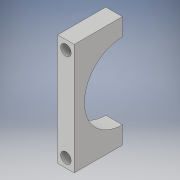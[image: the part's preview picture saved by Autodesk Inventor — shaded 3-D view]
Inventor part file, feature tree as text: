
AUTODESK INVENTOR PART (.ipt)
format: ipt  version: 2019 (Build 230136000, 136)  size: 118,272 bytes
history: native  units: mm
features: sketch x3, extrude x2, hole x1
ambient origin geometry x8: Origin, YZ Plane, XZ Plane, XY Plane, X Axis, Y Axis, Z Axis, Center Point
bodies: Body1 (feature_tree)
feature tree (6):
  sketch  "Sketch1"  dims[d2=50.0mm d7=5.5mm]
  extrude  "Extrusion4"  Depth=5.5mm
  hole  "Hole3"  [1 undecoded]
  extrude  "Extrusion5"  Depth=5.5mm
  sketch  "Sketch6"  dims[d8=37.0mm d9=31.0mm]
  sketch  "Sketch7"  dims[d10=3.0mm d11=2.75mm d45=5.5mm d46=37.0mm d47=31.0mm d48=3.0mm d49=2.75mm d50=16.0mm d51=0.0mm d52=3.5mm d53=6.0mm d54=4.0mm d55=2.0mm d56=90.0deg d57=8.0mm d58=20.594885mm d59=25.25mm d60=5.5mm d61=0.0mm]
note: 1 required parameter value undecoded (feature->parameter linkage not recoverable at this tier; creation-order binding heuristic only, values carry confidence <= 0.55)
